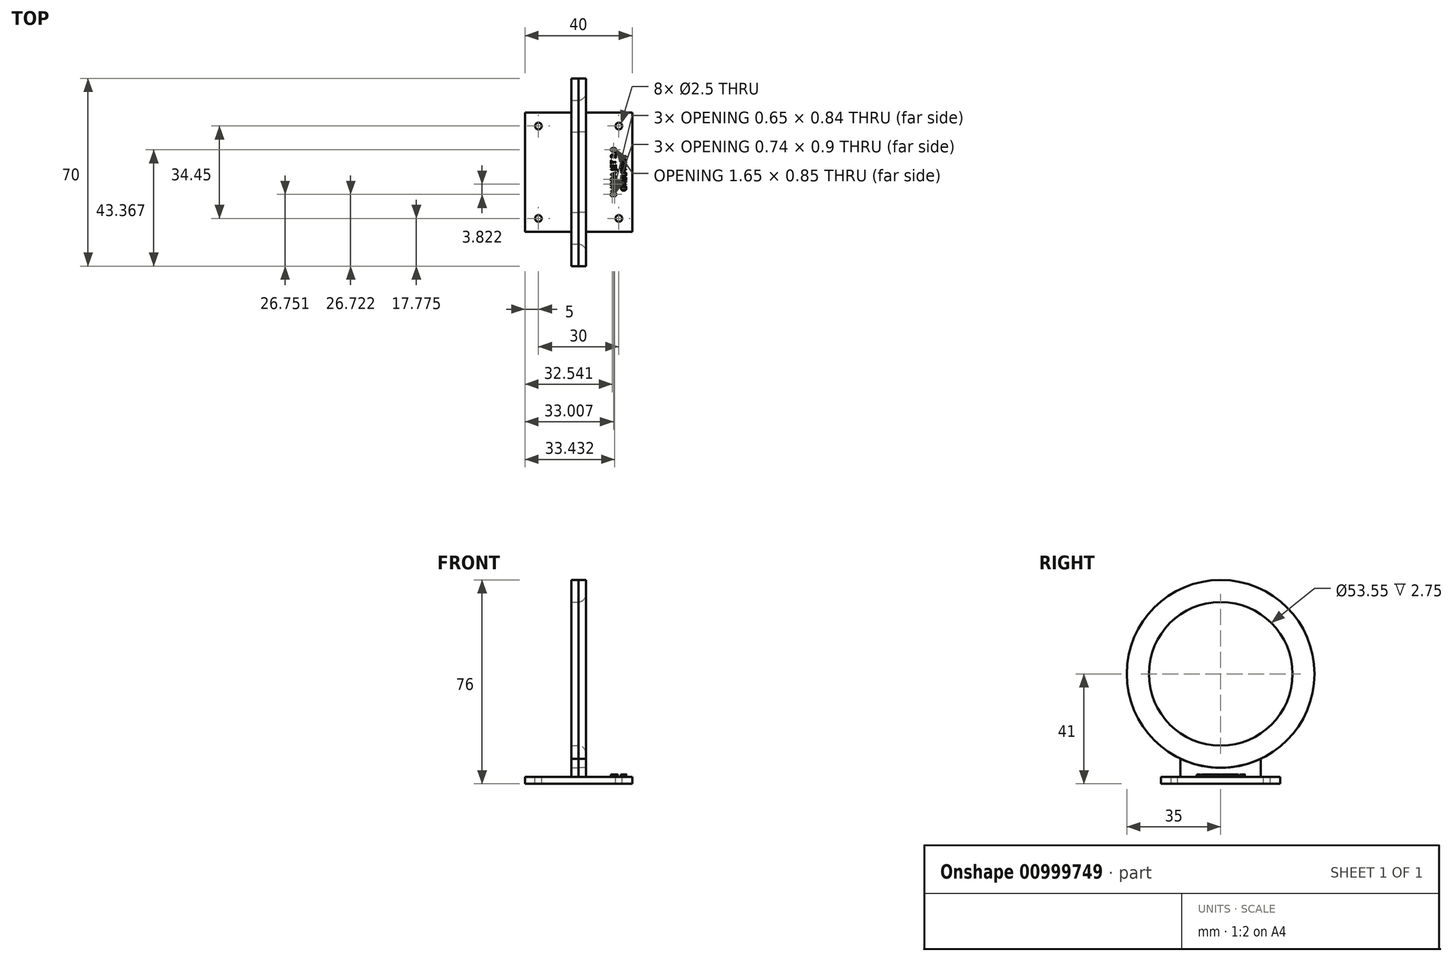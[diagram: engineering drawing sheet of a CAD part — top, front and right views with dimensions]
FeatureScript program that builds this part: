
annotation { "Feature Type Name" : "Feature", "Feature Type Description" : "" }
export const myFeature = defineFeature(function(context is Context, id is Id, definition is map)
    precondition{}
    {
        {
            var Q0;
            Q0=qCreatedBy(makeId("Top.planeOp"),FACE);
            var sketch = newSketch(context, id + "F0", { "sketchPlane" : qUnion([Q0])});
            skLineSegment(sketch, "E0.bottom", {"start": v(0, 0) * mm, "end": v(20, 0) * mm});
            skLineSegment(sketch, "E0.top", {"start": v(0, 22.22) * mm, "end": v(20, 22.22) * mm});
            skLineSegment(sketch, "E0.left", {"start": v(0, 0) * mm, "end": v(0, 22.22) * mm});
            skLineSegment(sketch, "E0.right", {"start": v(20, 0) * mm, "end": v(20, 22.23) * mm});
            skSolve(sketch);
        }
        {
            var Q0;
            Q0 = qSketchRegion(id + "F0", true);
            extrude(context, id + "F1", {"entities" : qUnion([Q0]), "depth" : 2.54 * mm, "offsetDistance" : 25.4 * mm});
        }
        {
            var Q0;
            Q0=qCreatedBy(makeId("Right.planeOp"),FACE);
            var sketch = newSketch(context, id + "F2", { "sketchPlane" : qUnion([Q0])});
            skLineSegment(sketch, "E1", {"start": v(0, 0) * mm, "end": v(0, 0) * mm});
            skCircle(sketch, "E2", {"center": v(0, 41) * mm, "radius": 35 * mm});
            skCircle(sketch, "E3", {"center": v(0, 41) * mm, "radius": 26.78 * mm});
            skLineSegment(sketch, "E4", {"start": v(0, 41) * mm, "end": v(0, 0) * mm});
            skSolve(sketch);
        }
        {
            var Q0;
            Q0=makeQuery(id+"F1.opExtrude","SWEPT_BODY",BODY,{"disambiguationData":[OSD([sQuery(id+"F0.wireOp",EDGE,"E0.bottom"),sQuery(id+"F0.wireOp",EDGE,"E0.top"),sQuery(id+"F0.wireOp",EDGE,"E0.left"),sQuery(id+"F0.wireOp",EDGE,"E0.right")])]});
            var Q1;
            Q1=qCreatedBy(makeId("Right.planeOp"),FACE);
            mirror(context, id + "F3", {"operationType" : NewBodyOperationType.ADD, "entities" : qUnion([Q0]), "mirrorPlane" : qUnion([Q1])});
        }
        {
            var Q0;
            Q0=makeQuery(id+"F1.opExtrude","SWEPT_BODY",BODY,{"disambiguationData":[OSD([sQuery(id+"F0.wireOp",EDGE,"E0.bottom"),sQuery(id+"F0.wireOp",EDGE,"E0.top"),sQuery(id+"F0.wireOp",EDGE,"E0.left"),sQuery(id+"F0.wireOp",EDGE,"E0.right")])]});
            var Q1;
            Q1=qCreatedBy(makeId("Front.planeOp"),FACE);
            mirror(context, id + "F4", {"operationType" : NewBodyOperationType.ADD, "entities" : qUnion([Q0]), "mirrorPlane" : qUnion([Q1])});
        }
        {
            var Q0;
            Q0 = qSketchRegion(id + "F2", true);
            extrude(context, id + "F5", {"entities" : qUnion([Q0]), "depth" : 2.75 * mm, "offsetDistance" : 25 * mm});
        }
        {
            var Q0;
            Q0=makeQuery(id+"F5.opExtrude","SWEPT_BODY",BODY,{"disambiguationData":[OSD([sQuery(id+"F2.wireOp",EDGE,"E2"),sQuery(id+"F2.wireOp",EDGE,"E3")])]});
            var Q1;
            Q1=qCreatedBy(makeId("Right.planeOp"),FACE);
            mirror(context, id + "F6", {"operationType" : NewBodyOperationType.ADD, "entities" : qUnion([Q0]), "mirrorPlane" : qUnion([Q1])});
        }
        {
            var Q0;
            Q0=qCreatedBy(makeId("Right.planeOp"),FACE);
            var sketch = newSketch(context, id + "F7", { "sketchPlane" : qUnion([Q0])});
            skLineSegment(sketch, "E5", {"start": v(-15, 2.54) * mm, "end": v(15, 2.54) * mm});
            skPoint(sketch, "E6", {"position": v(0, 41) * mm});
            skArc(sketch, "E7", {"start": v(15, 9.38) * mm, "mid": v(0, 6) * mm, "end": v(-15, 9.38) * mm});
            skLineSegment(sketch, "E8", {"start": v(15, 9.38) * mm, "end": v(15, 2.54) * mm});
            skLineSegment(sketch, "E9", {"start": v(-15, 9.38) * mm, "end": v(-15, 2.54) * mm});
            skSolve(sketch);
        }
        {
            var Q0;
            Q0 = qSketchRegion(id + "F7", true);
            extrude(context, id + "F8", {"entities" : qUnion([Q0]), "depth" : 2.75 * mm, "offsetDistance" : 25 * mm});
        }
        {
            var Q0;
            Q0=makeQuery(id+"F1.opExtrude","SWEPT_BODY",BODY,{"disambiguationData":[OSD([sQuery(id+"F0.wireOp",EDGE,"E0.bottom"),sQuery(id+"F0.wireOp",EDGE,"E0.top"),sQuery(id+"F0.wireOp",EDGE,"E0.left"),sQuery(id+"F0.wireOp",EDGE,"E0.right")])]});
            var Q1;
            Q1=makeQuery(id+"F8.opExtrude","SWEPT_BODY",BODY,{"disambiguationData":[OSD([sQuery(id+"F7.wireOp",EDGE,"E5"),sQuery(id+"F7.wireOp",EDGE,"E7"),sQuery(id+"F7.wireOp",EDGE,"E8"),sQuery(id+"F7.wireOp",EDGE,"E9")])]});
            var Q2;
            Q2=qCreatedBy(makeId("Right.planeOp"),FACE);
            mirror(context, id + "F9", {"entities" : qUnion([Q0, Q1]), "mirrorPlane" : qUnion([Q2])});
        }
        {
            var Q0;
            Q0=makeQuery(id+"F5.opExtrude","CAP_EDGE",EDGE,{"disambiguationData":[OSD([sQuery(id+"F2.wireOp",EDGE,"E3")])],"isStart":false});
            fillet(context, id + "F10", {"entities" : qUnion([Q0]), "radius" : 3 * mm, "tangentPropagation" : true, "allowEdgeOverflow" : false});
        }
        {
            var Q0;
            {var subQ0=makeQuery(id+"F1.opExtrude","CAP_FACE",FACE,{"disambiguationData":[OSD([sQuery(id+"F0.wireOp",EDGE,"E0.bottom"),sQuery(id+"F0.wireOp",EDGE,"E0.top"),sQuery(id+"F0.wireOp",EDGE,"E0.left"),sQuery(id+"F0.wireOp",EDGE,"E0.right")])],"isStart":false});var subQ1=makeQuery(id+"F3.boolean.opBoolean","MERGE",FACE,{"derivedFrom":[subQ0,makeQuery(id+"F3.opPattern","COPY",FACE,{"derivedFrom":subQ0,"instanceName":"1"})]});Q0=makeQuery(id+"F4.boolean.opBoolean","MERGE",FACE,{"derivedFrom":[subQ1,makeQuery(id+"F4.opPattern","COPY",FACE,{"derivedFrom":subQ1,"instanceName":"1"})]});}
            var sketch = newSketch(context, id + "F11", { "sketchPlane" : qUnion([Q0])});
            skCircle(sketch, "E10", {"center": v(-15, -17.22) * mm, "radius": 1.25 * mm});
            skCircle(sketch, "E11.MirrorC", {"center": v(-15, 17.22) * mm, "radius": 1.25 * mm});
            skCircle(sketch, "E12.MirrorC", {"center": v(15, -17.22) * mm, "radius": 1.25 * mm});
            skCircle(sketch, "E13.MirrorC", {"center": v(15, 17.22) * mm, "radius": 1.25 * mm});
            skSolve(sketch);
        }
        {
            var Q0;
            Q0 = qSketchRegion(id + "F11", true);
            extrude(context, id + "F12", {"entities" : qUnion([Q0]), "operationType" : NewBodyOperationType.REMOVE, "oppositeDirection" : true, "depth" : 25 * mm, "offsetDistance" : 25 * mm});
        }
        {
            var Q0;
            {var subQ0=makeQuery(id+"F1.opExtrude","CAP_FACE",FACE,{"disambiguationData":[OSD([sQuery(id+"F0.wireOp",EDGE,"E0.bottom"),sQuery(id+"F0.wireOp",EDGE,"E0.top"),sQuery(id+"F0.wireOp",EDGE,"E0.left"),sQuery(id+"F0.wireOp",EDGE,"E0.right")])],"isStart":false});var subQ1=makeQuery(id+"F3.boolean.opBoolean","MERGE",FACE,{"derivedFrom":[subQ0,makeQuery(id+"F3.opPattern","COPY",FACE,{"derivedFrom":subQ0,"instanceName":"1"})]});Q0=makeQuery(id+"F9.opPattern","COPY",FACE,{"derivedFrom":makeQuery(id+"F4.boolean.opBoolean","MERGE",FACE,{"derivedFrom":[subQ1,makeQuery(id+"F4.opPattern","COPY",FACE,{"derivedFrom":subQ1,"instanceName":"1"})]}),"instanceName":"1"});}
            var sketch = newSketch(context, id + "F13", { "sketchPlane" : qUnion([Q0])});
            skText(sketch, "E14", { "text": "BUBBA JET 2.0\n   GREUTERT", "fontName": "OpenSans-Regular.ttf"});
            const initialGuessF13  = {"E14": [0.014, -0.0092, 0, 1, 0.002]};
            skSetInitialGuess(sketch, initialGuessF13);
            skSolve(sketch);
        }
        {
            var Q0;
            Q0 = qSketchRegion(id + "F13", true);
            extrude(context, id + "F14", {"entities" : qUnion([Q0]), "depth" : 1 * mm, "offsetDistance" : 25 * mm});
        }
    });
